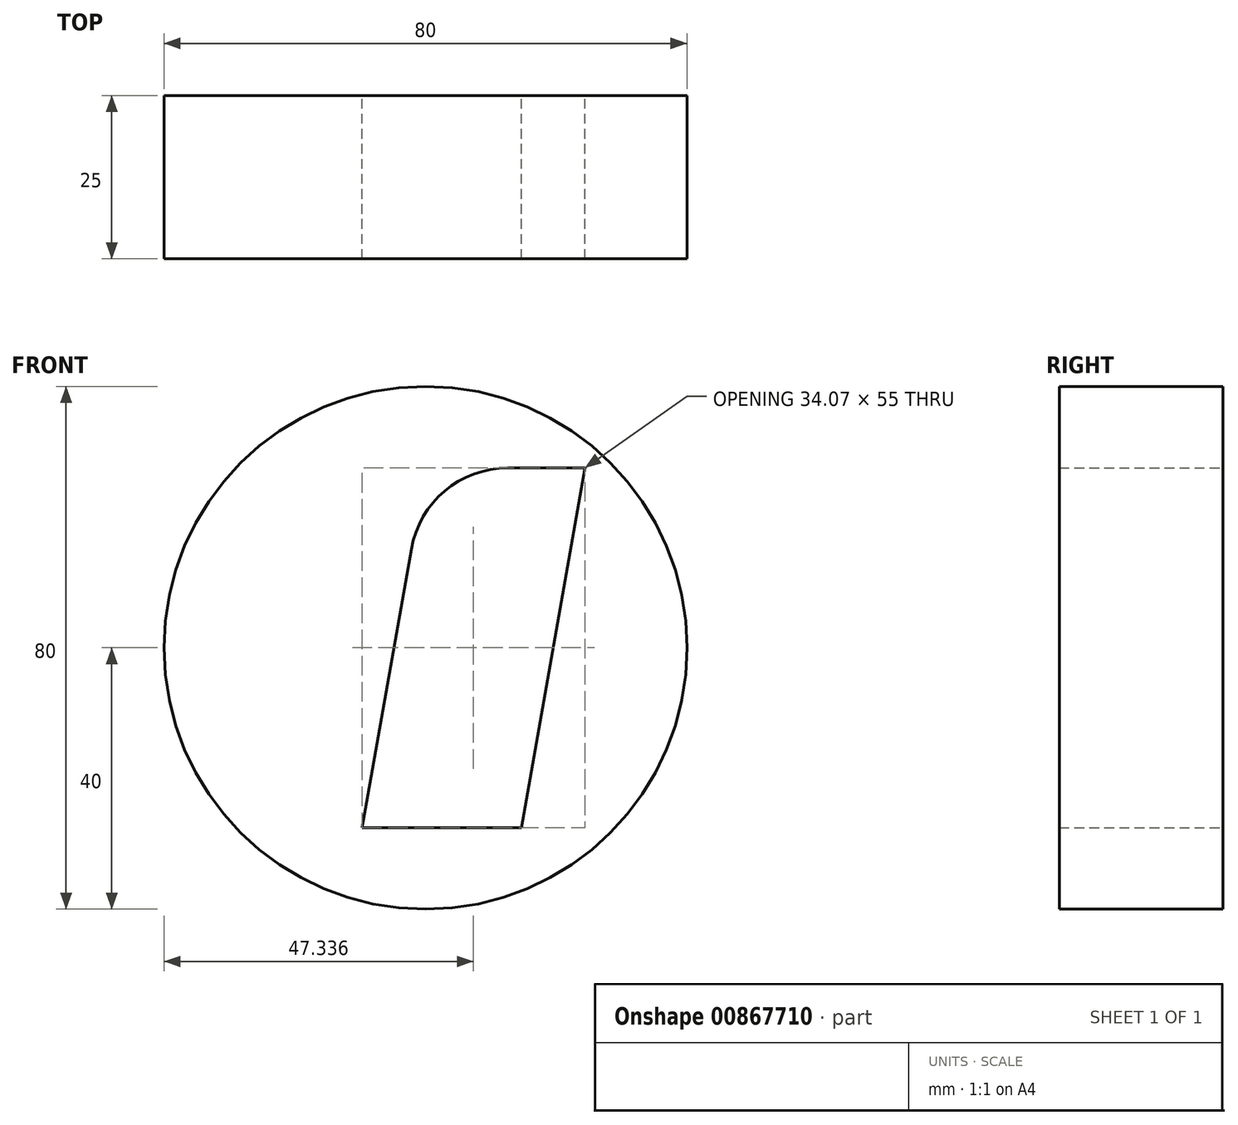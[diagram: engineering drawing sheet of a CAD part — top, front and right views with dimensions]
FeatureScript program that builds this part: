
annotation { "Feature Type Name" : "Feature", "Feature Type Description" : "" }
export const myFeature = defineFeature(function(context is Context, id is Id, definition is map)
    precondition{}
    {
        {
            var Q0;
            Q0=qCreatedBy(makeId("Front.planeOp"),FACE);
            var sketch = newSketch(context, id + "F0", { "sketchPlane" : qUnion([Q0])});
            skCircle(sketch, "E0", {"center": v(0, 0) * mm, "radius": 40 * mm});
            skLineSegment(sketch, "E1", {"start": v(14.67, -27.5) * mm, "end": v(24.37, 27.5) * mm});
            skLineSegment(sketch, "E2", {"start": v(24.37, 27.5) * mm, "end": v(12.59, 27.5) * mm});
            skLineSegment(sketch, "E3", {"start": v(-2.19, 15.1) * mm, "end": v(-9.7, -27.5) * mm});
            skLineSegment(sketch, "E4", {"start": v(-9.7, -27.5) * mm, "end": v(14.67, -27.5) * mm});
            skPoint(sketch, "E5.visualSharp", {"position": v(0, 27.5) * mm});
            skArc(sketch, "E5.filletArc", {"start": v(12.59, 27.5) * mm, "mid": v(2.94, 24) * mm, "end": v(-2.19, 15.1) * mm});
            skSolve(sketch);
        }
        {
            var Q0;
            Q0=makeQuery(id+"F0.imprint","IMPRINT",FACE,{"disambiguationData":[TD([[makeQuery(id+"F0.imprint","IMPRINT",EDGE,{"derivedFrom":sQuery(id+"F0.wireOp",EDGE,"E0")}),1.0]])]});
            extrude(context, id + "F1", {"entities" : qUnion([Q0]), "depth" : 25 * mm, "offsetDistance" : 25 * mm});
        }
    });
